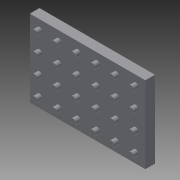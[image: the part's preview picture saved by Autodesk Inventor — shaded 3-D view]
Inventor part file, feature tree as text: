
AUTODESK INVENTOR PART (.ipt)
format: ipt  version: 2015 (Build 190159000, 159)  size: 129,024 bytes
history: native  units: in
note: dims shown in document units (in); Inventor stores cm internally (conversion verified against a paired STEP export)
features: extrude x2, sketch x2
ambient origin geometry x8: Origin, YZ Plane, XZ Plane, XY Plane, X Axis, Y Axis, Z Axis, Center Point
bodies: Solid1 (feature_tree)
feature tree (4):
  extrude  "Extrusion1"  Depth=6.0in
  extrude  "Extrusion2"  Depth=0.25in
  sketch  "Sketch1"  dims[d0=4.0in d1=6.0in]
  sketch  "Sketch3"  dims[d2=0.5in d3=0.0in d5=0.3in d6=0.5in d7=0.5in d8=1.5748in d10=1.0in d11=2.3622in d13=1.0in d16=0.25in d17=0.0in]
